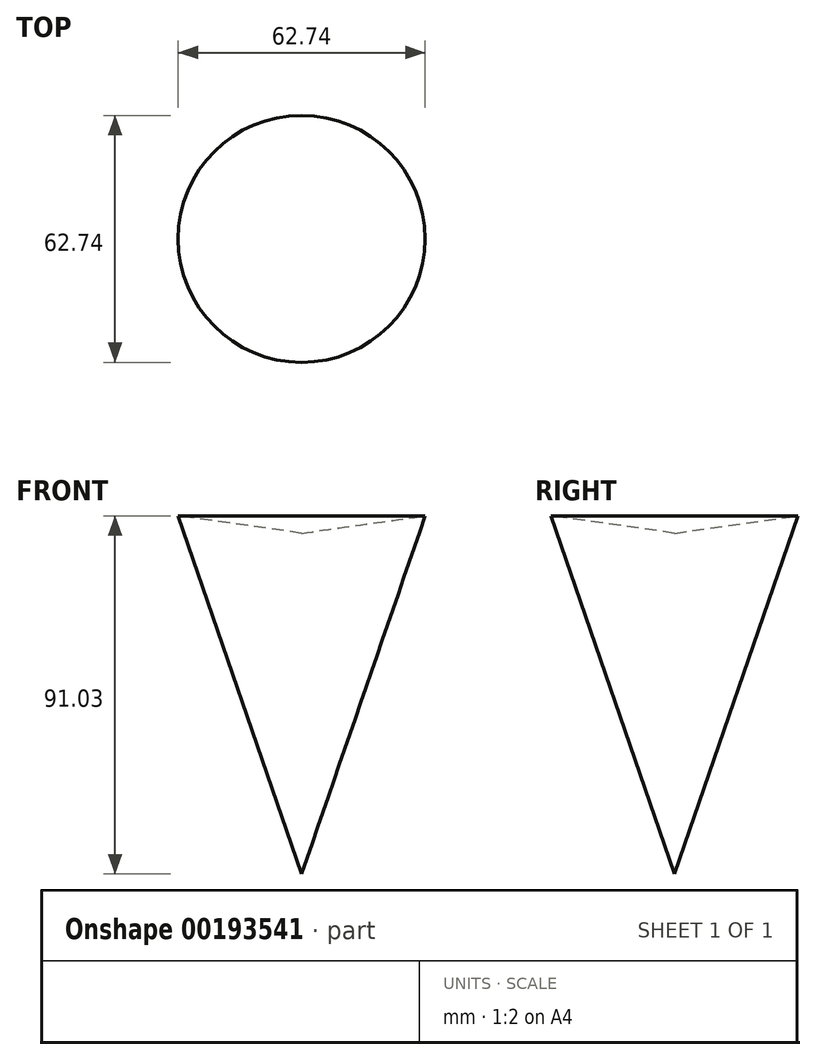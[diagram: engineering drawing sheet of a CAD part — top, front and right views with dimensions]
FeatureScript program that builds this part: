
annotation { "Feature Type Name" : "Feature", "Feature Type Description" : "" }
export const myFeature = defineFeature(function(context is Context, id is Id, definition is map)
    precondition{}
    {
        {
            var Q0;
            Q0=qCreatedBy(makeId("Front.planeOp"),FACE);
            var sketch = newSketch(context, id + "F0", { "sketchPlane" : qUnion([Q0])});
            skLineSegment(sketch, "E0", {"start": v(-31.37, 27.62) * mm, "end": v(0, -63.4) * mm});
            skLineSegment(sketch, "E1", {"start": v(-31.37, 27.62) * mm, "end": v(0, 23.2) * mm});
            skLineSegment(sketch, "E2", {"start": v(0, 23.2) * mm, "end": v(0, -63.4) * mm});
            skSolve(sketch);
        }
        {
            var Q0;
            Q0 = qSketchRegion(id + "F0", true);
            var Q1;
            Q1=sQuery(id+"F0.wireOp",EDGE,"E2");
            revolve(context, id + "F1", {"entities" : qUnion([Q0]), "axis" : qUnion([Q1]), "revolveType" : RevolveType.FULL});
        }
    });
